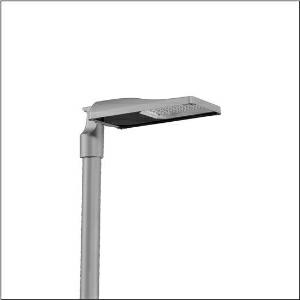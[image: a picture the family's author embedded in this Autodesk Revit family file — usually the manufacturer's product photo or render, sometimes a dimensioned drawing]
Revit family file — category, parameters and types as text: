
# Revit family: streetlight_sl_31_mini___st1_0a_5xh6d31b08ga_f949
name_source: partatom
category: Lighting Fixtures
units: mm (PartAtom-declared; Revit-internal decimal feet)

## family parameters
Cut with Voids When Loaded = No
Host = Face
Light Source = No
Part Type = Normal
Room Calculation Point = No
Round Connector Dimension = Use Diameter
Shared = No

## types (1)
- --- (1 x LED, 5710 lm, 37.3 W, 3000K)
    Apparent Load = 37 VA
    CIE Flux Codes = 37 72 97 100 100
    Color Rendering = 70
    Color Temperature = 3000K
    Default Elevation = 1800 mm
    Description = Streetlight SL 31 mini Easy, LST, Desk-Remote mast luminaire for post-top, side-entry; light control with lens of PMMA; light distribution: ST1.0a, direct asymmetric distribution, for standard-compliant lighting for roads and squares; LED: luminous flux: 5.710lm, light colour: 730, colour temperature: 3000K; luminous efficacy: 153,1lm/W; control: pre-setting: linear dimming characteristic, flexible luminous flux parameterisation, time-dependent luminous flux control, constant luminous flux control, power reduction, intelligent temperature release in ECG and LED module, overheat protection; luminaire housing, of diecast aluminium, SITECO metallic grey (DB 702S), corrosivity category C5 high according to DIN EN ISO 12944; cover of toughened safety glass, transparent, opened without tools; mast flange of diecast aluminium, SITECO metallic grey (DB 702S), spigot size: 76/60mm, mast flange included unmounted; with cable H07RN-F 5x 1.5mm², cable length: 6,5m, connection cable pre-assembled; mains connection: 220..240V, AC, 50/60Hz; power consumption (at start of service life): 37,3W / (at end of service life): 38,7W / (with reduced operation 50%): 17,5W; protection rating (complete): IP66; insulation class (complete): insulation class II (safety insulation); impact resistance: IK10; certification: CE, ENEC, ENEC+, VDE, UKCA; permissible operating ambient temperature for outdoor applications: -40..+50°C; packaging unit: 1 piece

Light Distribution: ST1.0a
    Height = 76 mm
    Lamp = 1 x LED
    Lamp Light Flux = 5710 lm
    Lamp Power = 37.3 W
    Lamp count = 1
    Length = 547 mm
    Luminous efficacy = 153 lm/W
    Manufacturer = Siteco
    ModVariant = No
    Model = 5XH6D31B08GA
    Number of Poles = 1
    OnlyDefault = Yes
    Power Factor = 1
    Product Name = Streetlight SL 31 mini | ST1.0a
    Product group = mast luminaire | pylon top
    ProductGroupID = 6100
    Protection Class = Protection class II
    Protection Degree = IP 66
    RLX_Detail_Level = 1
    RLX_Emergency_Light_Flux = 0 lm
    RLX_Emergency_Type = 0
    RLX_Emergency_Type_DB = No
    RlxData = <blob elided: 39577 chars, md5=259b7424>
    Socket = socket
    Standby Power = 0 W
    System Light Flux = 5710 lm
    System Power = 37 W
    Type Comments = factory setting: luminous flux: 100 % | dim-lin: 254 | 386 mA
    Type Image = l_1300326.jpg
    URL = http://relux.com
    VarID = @adj_060941
    Voltage = 0 V
    Weight = 0.00 kg
    Width = 265 mm

## geometry (parser evidence)
native form markers: Blend x4, Sweep x9
no freeform markers — native parametric forms only
